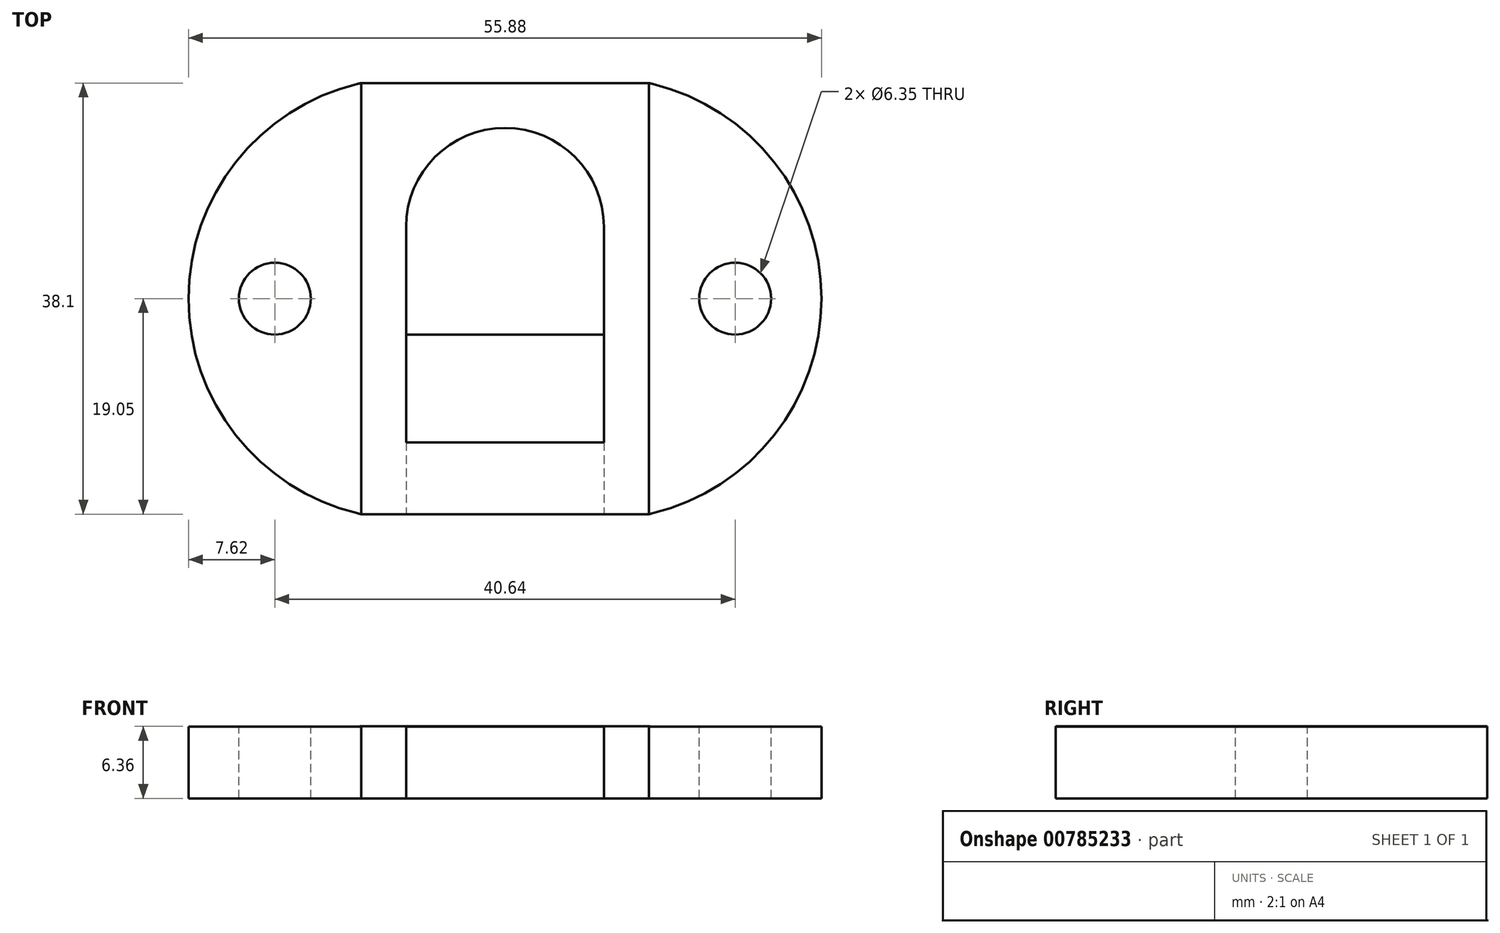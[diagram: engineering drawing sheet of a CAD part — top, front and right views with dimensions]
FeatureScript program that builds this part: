
annotation { "Feature Type Name" : "Feature", "Feature Type Description" : "" }
export const myFeature = defineFeature(function(context is Context, id is Id, definition is map)
    precondition{}
    {
        {
            var Q0;
            Q0=qCreatedBy(makeId("Top.planeOp"),FACE);
            var sketch = newSketch(context, id + "F0", { "sketchPlane" : qUnion([Q0])});
            skLineSegment(sketch, "E0.top", {"start": v(12.7, -25.4) * mm, "end": v(-12.7, -25.4) * mm});
            skPoint(sketch, "E0.middle", {"position": v(0, 0) * mm});
            skCircle(sketch, "E1", {"center": v(0, 0) * mm, "radius": 8.73 * mm});
            skLineSegment(sketch, "E2", {"start": v(-8.73, 0) * mm, "end": v(-8.73, -19.05) * mm});
            skLineSegment(sketch, "E3.bottom", {"start": v(-8.73, -19.05) * mm, "end": v(8.73, -19.05) * mm});
            skLineSegment(sketch, "E3.left", {"start": v(-8.73, -19.05) * mm, "end": v(-8.73, 0) * mm});
            skLineSegment(sketch, "E3.right", {"start": v(8.73, -19.05) * mm, "end": v(8.73, 0) * mm});
            skLineSegment(sketch, "E4", {"start": v(-12.7, 12.7) * mm, "end": v(12.7, 12.7) * mm});
            skLineSegment(sketch, "E5", {"start": v(12.7, 12.7) * mm, "end": v(12.7, -25.4) * mm});
            skLineSegment(sketch, "E6", {"start": v(-12.7, -25.4) * mm, "end": v(-12.7, 12.7) * mm});
            skSolve(sketch);
        }
        {
            var Q0;
            Q0 = qSketchRegion(id + "F0", true);
            extrude(context, id + "F1", {"entities" : qUnion([Q0]), "depth" : 2 / 203.2 * mm, "offsetDistance" : 25.4 * mm});
        }
        {
            var Q0;
            Q0=makeQuery(id+"F1.opExtrude","CAP_FACE",FACE,{"disambiguationData":[OSD([sQuery(id+"F0.wireOp",EDGE,"E1"),sQuery(id+"F0.wireOp",EDGE,"E3.bottom"),sQuery(id+"F0.wireOp",EDGE,"E3.left"),sQuery(id+"F0.wireOp",EDGE,"E3.right"),sQuery(id+"F0.wireOp",EDGE,"E4"),sQuery(id+"F0.wireOp",EDGE,"E5"),sQuery(id+"F0.wireOp",EDGE,"E0.top"),sQuery(id+"F0.wireOp",EDGE,"E6")])],"isStart":true});
            var sketch = newSketch(context, id + "F2", { "sketchPlane" : qUnion([Q0])});
            skLineSegment(sketch, "E7.bottom", {"start": v(12.7, -12.7) * mm, "end": v(-12.7, -12.7) * mm});
            skCircle(sketch, "E8", {"center": v(-20.32, 6.35) * mm, "radius": 3.18 * mm});
            skArc(sketch, "E9", {"start": v(-12.7, 25.4) * mm, "mid": v(-27.94, 6.35) * mm, "end": v(-12.7, -12.7) * mm});
            skLineSegment(sketch, "E10", {"start": v(8.73, 19.05) * mm, "end": v(8.73, 25.4) * mm});
            skPoint(sketch, "E10.endSnap0", {"position": v(0, 25.4) * mm});
            skLineSegment(sketch, "E11", {"start": v(-8.73, 25.4) * mm, "end": v(-8.73, 19.05) * mm});
            skLineSegment(sketch, "E12", {"start": v(12.7, 25.4) * mm, "end": v(8.73, 25.4) * mm});
            skLineSegment(sketch, "E13", {"start": v(8.73, 19.05) * mm, "end": v(8.73, 9.53) * mm});
            skLineSegment(sketch, "E14", {"start": v(8.73, 9.53) * mm, "end": v(-8.73, 9.53) * mm});
            skLineSegment(sketch, "E15", {"start": v(-8.73, 9.53) * mm, "end": v(-8.73, 19.05) * mm});
            skCircle(sketch, "E16", {"center": v(20.32, 6.35) * mm, "radius": 3.18 * mm});
            skArc(sketch, "E17", {"start": v(12.7, -12.7) * mm, "mid": v(27.94, 6.35) * mm, "end": v(12.7, 25.4) * mm});
            skSolve(sketch);
        }
        {
            var Q0;
            Q0=makeQuery(id+"F2.imprint","IMPRINT",FACE,{"disambiguationData":[TD([[makeQuery(id+"F2.imprint","IMPRINT",EDGE,{"derivedFrom":sQuery(id+"F2.wireOp",EDGE,"E16")}),-1.0]])]});
            var Q1;
            Q1=makeQuery(id+"F2.imprint","IMPRINT",FACE,{"disambiguationData":[TD([[makeQuery(id+"F2.imprint","IMPRINT",EDGE,{"derivedFrom":sQuery(id+"F2.wireOp",EDGE,"E8")}),-1.0]])]});
            var Q2;
            Q2=makeQuery(id+"F2.imprint","IMPRINT",FACE,{"disambiguationData":[TD([[makeQuery(id+"F2.imprint","IMPRINT",EDGE,{"derivedFrom":sQuery(id+"F2.wireOp",EDGE,"E7.bottom")}),1.0]])]});
            var Q3;
            {var subQ0=sQuery(id+"F2.wireOp",EDGE,"E14");Q3=makeQuery(id+"F2.imprint","IMPRINT",FACE,{"disambiguationData":[TD([[makeQuery(id+"F2.imprint","IMPRINT",EDGE,{"derivedFrom":subQ0}),1.0]])]});}
            extrude(context, id + "F3", {"entities" : qUnion([Q0, Q1, Q2, Q3]), "operationType" : NewBodyOperationType.ADD, "depth" : 6.35 * mm, "offsetDistance" : 25.4 * mm});
        }
        {
            var Q0;
            Q0=makeQuery(id+"F1.opExtrude","CAP_EDGE",EDGE,{"disambiguationData":[OSD([sQuery(id+"F0.wireOp",EDGE,"E5")])],"isStart":true});
            var Q1;
            Q1=makeQuery(id+"F1.opExtrude","CAP_EDGE",EDGE,{"disambiguationData":[OSD([sQuery(id+"F0.wireOp",EDGE,"E6")])],"isStart":true});
            var Q2;
            Q2=makeQuery(id+"F3.opExtrude","CAP_EDGE",EDGE,{"disambiguationData":[OSD([sQuery(id+"F2.wireOp",EDGE,"E11"),sQuery(id+"F2.wireOp",EDGE,"E15")])],"isStart":true});
            var Q3;
            Q3=makeQuery(id+"F3.opExtrude","CAP_EDGE",EDGE,{"disambiguationData":[OSD([sQuery(id+"F2.wireOp",EDGE,"E10"),sQuery(id+"F2.wireOp",EDGE,"E13")])],"isStart":true});
            fillet(context, id + "F4", {"entities" : qUnion([Q0, Q1, Q2, Q3]), "radius" : 5.08 * mm, "tangentPropagation" : true, "allowEdgeOverflow" : false});
        }
    });
